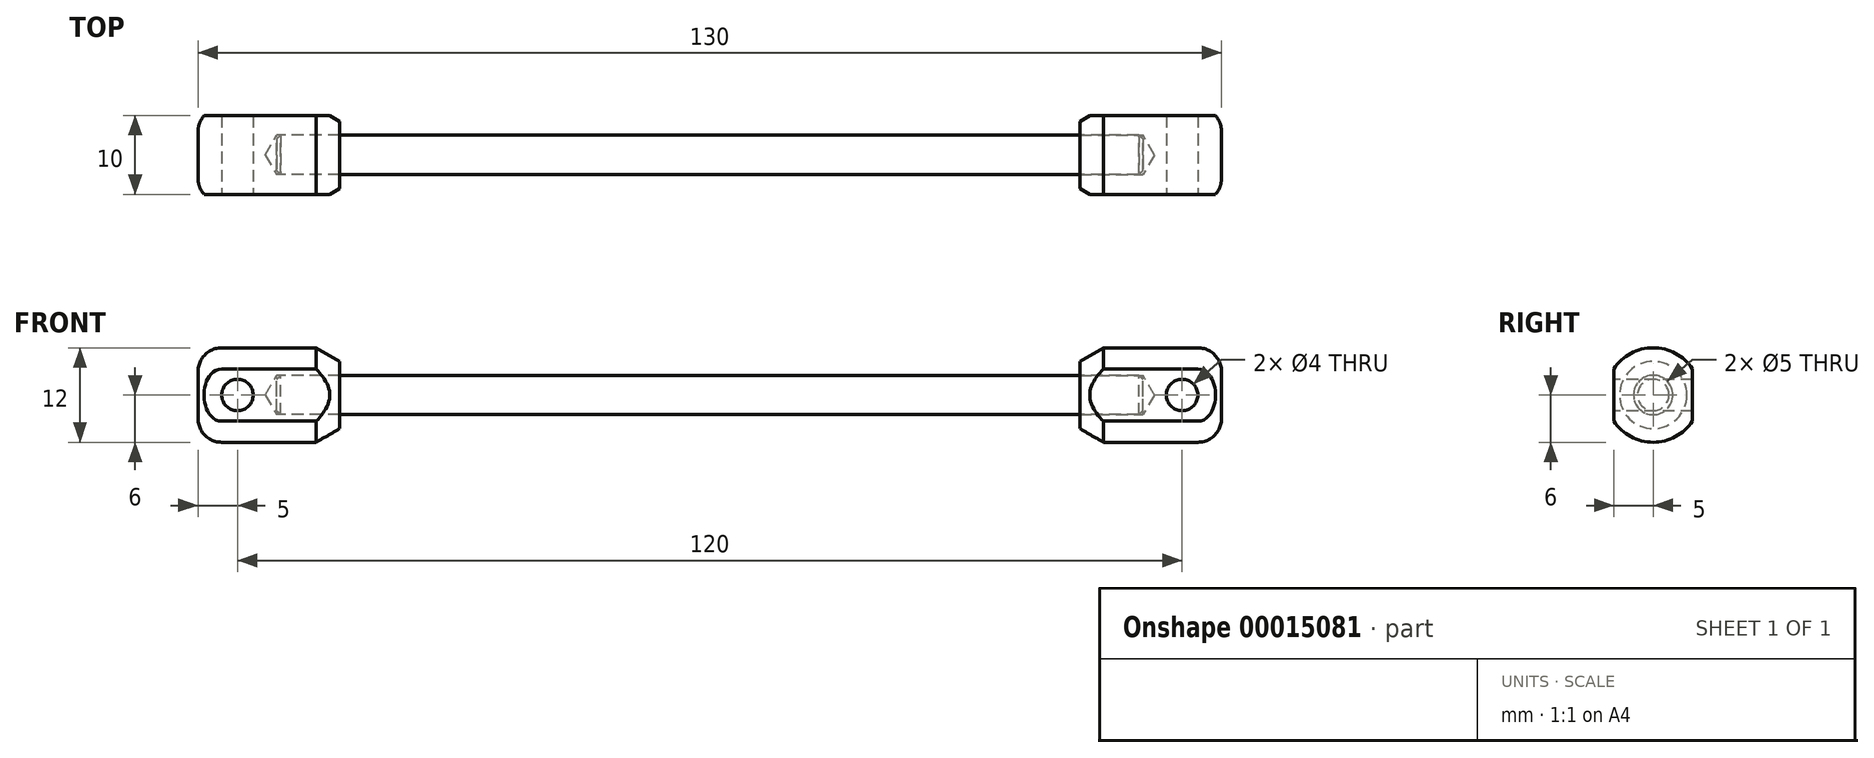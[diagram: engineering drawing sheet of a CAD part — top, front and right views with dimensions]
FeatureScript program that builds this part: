
annotation { "Feature Type Name" : "Feature", "Feature Type Description" : "" }
export const myFeature = defineFeature(function(context is Context, id is Id, definition is map)
    precondition{}
    {
        {
            var Q0;
            Q0=qCreatedBy(makeId("Right.planeOp"),FACE);
            var sketch = newSketch(context, id + "F0", { "sketchPlane" : qUnion([Q0])});
            skCircle(sketch, "E0", {"center": v(0, 0) * mm, "radius": 2.5 * mm});
            skSolve(sketch);
        }
        {
            var Q0;
            Q0=makeQuery(id+"F0.imprint","IMPRINT",FACE,{"disambiguationData":[TD([[makeQuery(id+"F0.imprint","IMPRINT",EDGE,{"derivedFrom":sQuery(id+"F0.wireOp",EDGE,"E0")}),1.0]])]});
            extrude(context, id + "F1", {"entities" : qUnion([Q0]), "depth" : (110 / 2) * mm});
        }
        {
            var Q0;
            Q0=makeQuery(id+"F1.opExtrude","CAP_EDGE",EDGE,{"disambiguationData":[OSD([sQuery(id+"F0.wireOp",EDGE,"E0")])],"isStart":false});
            chamfer(context, id + "F2", {"entities" : qUnion([Q0]), "width" : .5 * mm, "tangentPropagation" : true});
        }
        {
            var Q0;
            Q0=makeQuery(id+"F1.opExtrude","SWEPT_BODY",BODY,{"disambiguationData":[OSD([sQuery(id+"F0.wireOp",EDGE,"E0")])]});
            var Q1;
            Q1=makeQuery(id+"F1.opExtrude","CAP_FACE",FACE,{"disambiguationData":[OSD([sQuery(id+"F0.wireOp",EDGE,"E0")])],"isStart":true});
            mirror(context, id + "F3", {"operationType" : NewBodyOperationType.ADD, "entities" : qUnion([Q0]), "mirrorPlane" : qUnion([Q1])});
        }
        {
            var Q0;
            Q0=qCreatedBy(makeId("Front.planeOp"),FACE);
            var sketch = newSketch(context, id + "F4", { "sketchPlane" : qUnion([Q0])});
            skLineSegment(sketch, "E1", {"start": v(-54.5, 2.5) * mm, "end": v(54.5, 2.5) * mm});
            skLineSegment(sketch, "E2", {"start": v(54.5, -2.5) * mm, "end": v(-54.5, -2.5) * mm});
            skLineSegment(sketch, "E3", {"start": v(54.5, 2.5) * mm, "end": v(55, 2) * mm});
            skLineSegment(sketch, "E4", {"start": v(55, -2) * mm, "end": v(54.5, -2.5) * mm});
            skLineSegment(sketch, "E5.0", {"start": v(55, 2) * mm, "end": v(55, -2) * mm});
            skLineSegment(sketch, "E6", {"start": v(36.28, 0) * mm, "end": v(73.5, 0) * mm, "construction": true});
            skLineSegment(sketch, "E7", {"start": v(50, -6) * mm, "end": v(62, -6) * mm});
            skLineSegment(sketch, "E8", {"start": v(65, -3) * mm, "end": v(65, 0) * mm});
            skLineSegment(sketch, "E9", {"start": v(65, 0) * mm, "end": v(47, 0) * mm});
            skLineSegment(sketch, "E10", {"start": v(47, 0) * mm, "end": v(47, -2.5) * mm});
            skLineSegment(sketch, "E11", {"start": v(47, -2.5) * mm, "end": v(55, -2.5) * mm});
            skLineSegment(sketch, "E12", {"start": v(55, -2.5) * mm, "end": v(56.65, 0.25) * mm});
            skPoint(sketch, "E13.visualSharp", {"position": v(65, -6) * mm});
            skArc(sketch, "E13.filletArc", {"start": v(62, -6) * mm, "mid": v(64.12, -5.12) * mm, "end": v(65, -3) * mm});
            skLineSegment(sketch, "E14", {"start": v(50, -6) * mm, "end": v(47, -4.27) * mm});
            skLineSegment(sketch, "E15", {"start": v(47, -4.27) * mm, "end": v(47, -2.5) * mm});
            skSolve(sketch);
        }
        {
            var Q0;
            Q0=makeQuery(id+"F4.imprint","IMPRINT",FACE,{"disambiguationData":[TD([[makeQuery(id+"F4.imprint","IMPRINT",EDGE,{"derivedFrom":sQuery(id+"F4.wireOp",EDGE,"E7")}),1.0]])]});
            var Q1;
            Q1=sQuery(id+"F4.wireOp",EDGE,"E9");
            revolve(context, id + "F5", {"entities" : qUnion([Q0]), "axis" : qUnion([Q1]), "revolveType" : RevolveType.FULL});
        }
        {
            var Q0;
            Q0=qCreatedBy(makeId("Right.planeOp"),FACE);
            var sketch = newSketch(context, id + "F6", { "sketchPlane" : qUnion([Q0])});
            skLineSegment(sketch, "E16", {"start": v(0, 9.86) * mm, "end": v(0, -10.52) * mm, "construction": true});
            skLineSegment(sketch, "E17", {"start": v(-12.5, 0) * mm, "end": v(12.24, 0) * mm, "construction": true});
            skLineSegment(sketch, "E18.bottom", {"start": v(5, 9.7) * mm, "end": v(10.52, 9.7) * mm});
            skLineSegment(sketch, "E18.top", {"start": v(5, -9.8) * mm, "end": v(10.52, -9.8) * mm});
            skLineSegment(sketch, "E18.left", {"start": v(5, 9.7) * mm, "end": v(5, -9.8) * mm});
            skLineSegment(sketch, "E18.right", {"start": v(10.52, 9.7) * mm, "end": v(10.52, -9.8) * mm});
            skLineSegment(sketch, "E19.0.MirrorCS", {"start": v(-5, 9.7) * mm, "end": v(-5, -9.8) * mm});
            skLineSegment(sketch, "E19.1.MirrorCS", {"start": v(-5, 9.7) * mm, "end": v(-10.52, 9.7) * mm});
            skLineSegment(sketch, "E19.2.MirrorCS", {"start": v(-10.52, 9.7) * mm, "end": v(-10.52, -9.8) * mm});
            skLineSegment(sketch, "E20.0.MirrorCS", {"start": v(-5, -9.8) * mm, "end": v(-10.52, -9.8) * mm});
            skSolve(sketch);
        }
        {
            var Q0;
            Q0=makeQuery(id+"F6.imprint","IMPRINT",FACE,{"disambiguationData":[TD([[makeQuery(id+"F6.imprint","IMPRINT",EDGE,{"derivedFrom":sQuery(id+"F6.wireOp",EDGE,"E19.0.MirrorCS")}),-1.0]])]});
            var Q1;
            Q1=makeQuery(id+"F6.imprint","IMPRINT",FACE,{"disambiguationData":[TD([[makeQuery(id+"F6.imprint","IMPRINT",EDGE,{"derivedFrom":sQuery(id+"F6.wireOp",EDGE,"E18.bottom")}),-1.0]])]});
            extrude(context, id + "F7", {"entities" : qUnion([Q0, Q1]), "operationType" : NewBodyOperationType.REMOVE, "endBound" : BoundingType.THROUGH_ALL, "depth" : 25 * mm});
        }
        {
            var Q0;
            Q0=makeQuery(id+"F7.boolean.opBoolean","COPY",FACE,{"derivedFrom":makeQuery(id+"F7.opExtrude","SWEPT_FACE",FACE,{"disambiguationData":[OSD([sQuery(id+"F6.wireOp",EDGE,"E19.0.MirrorCS")])]})});
            var sketch = newSketch(context, id + "F8", { "sketchPlane" : qUnion([Q0])});
            skLineSegment(sketch, "E21", {"start": v(51.7, 0) * mm, "end": v(80.25, 0) * mm, "construction": true});
            skCircle(sketch, "E22", {"center": v(60, 0) * mm, "radius": 2 * mm});
            skSolve(sketch);
        }
        {
            var Q0;
            Q0=makeQuery(id+"F8.imprint","IMPRINT",FACE,{"disambiguationData":[TD([[makeQuery(id+"F8.imprint","IMPRINT",EDGE,{"derivedFrom":sQuery(id+"F8.wireOp",EDGE,"E22")}),1.0]])]});
            extrude(context, id + "F9", {"entities" : qUnion([Q0]), "operationType" : NewBodyOperationType.REMOVE, "endBound" : BoundingType.THROUGH_ALL, "oppositeDirection" : true, "depth" : 25 * mm});
        }
        {
            var Q0;
            Q0=makeQuery(id+"F5.opRevolve","SWEPT_BODY",BODY,{"disambiguationData":[OSD([sQuery(id+"F4.wireOp",EDGE,"E7"),sQuery(id+"F4.wireOp",EDGE,"E8"),sQuery(id+"F4.wireOp",EDGE,"E9"),sQuery(id+"F4.wireOp",EDGE,"E11"),sQuery(id+"F4.wireOp",EDGE,"E12"),sQuery(id+"F4.wireOp",EDGE,"E13.filletArc"),sQuery(id+"F4.wireOp",EDGE,"E14"),sQuery(id+"F4.wireOp",EDGE,"E15")])]});
            var Q1;
            Q1=qCreatedBy(makeId("Right.planeOp"),FACE);
            mirror(context, id + "F10", {"entities" : qUnion([Q0]), "mirrorPlane" : qUnion([Q1])});
        }
    });
